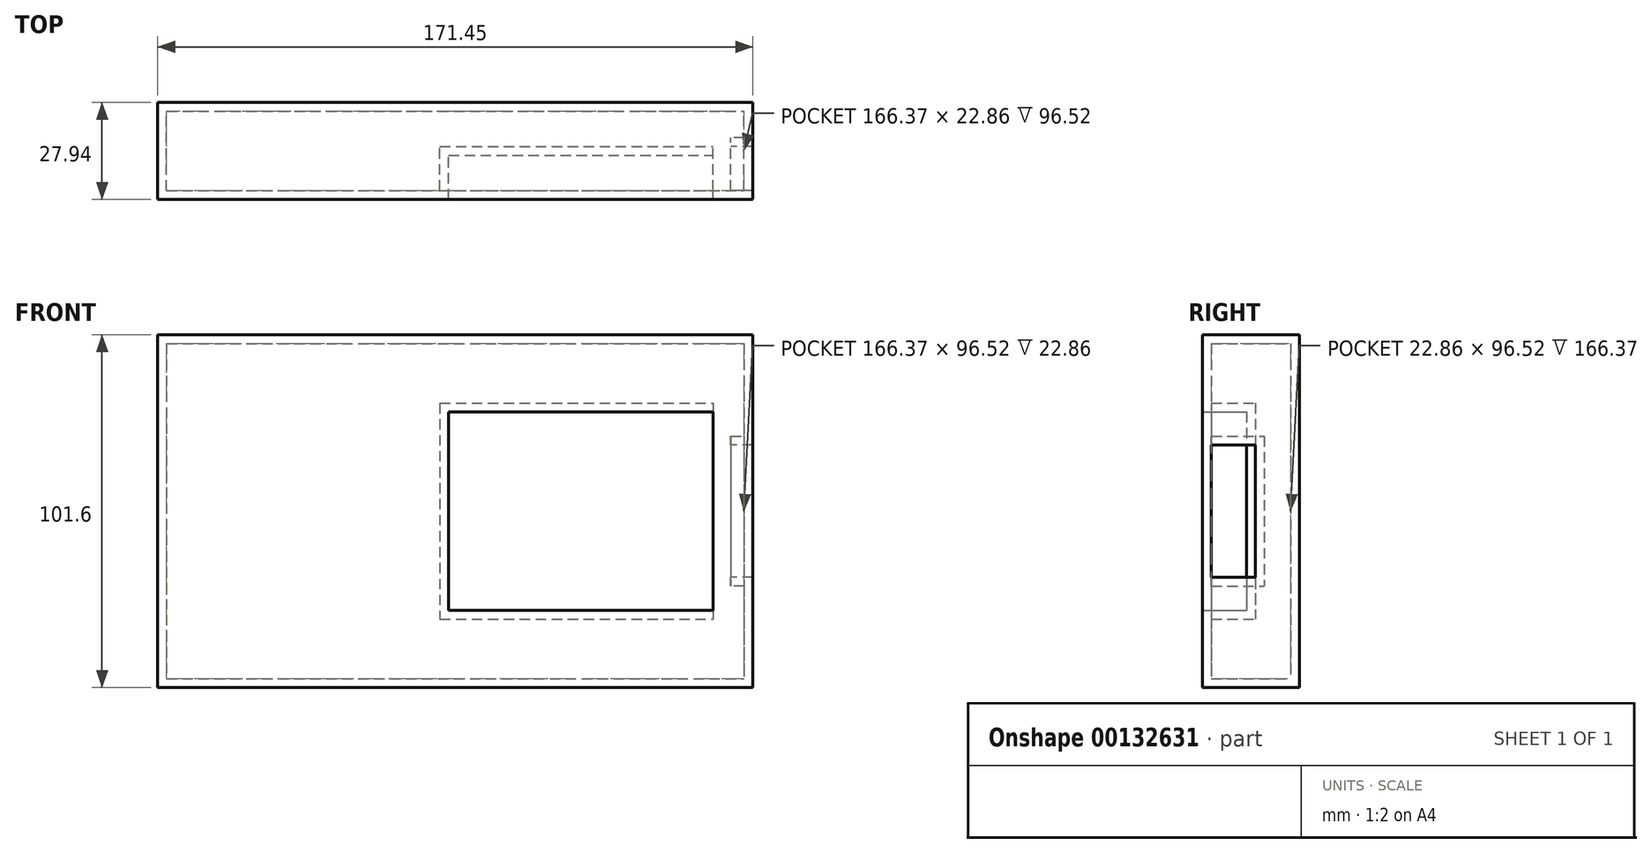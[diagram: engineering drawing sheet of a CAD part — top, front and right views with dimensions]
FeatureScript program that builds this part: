
annotation { "Feature Type Name" : "Feature", "Feature Type Description" : "" }
export const myFeature = defineFeature(function(context is Context, id is Id, definition is map)
    precondition{}
    {
        {
            var Q0;
            Q0=qCreatedBy(makeId("Front.planeOp"),FACE);
            var sketch = newSketch(context, id + "F0", { "sketchPlane" : qUnion([Q0])});
            skLineSegment(sketch, "E0.bottom", {"start": v(-70.48, 47.32) * mm, "end": v(94.62, 47.32) * mm});
            skLineSegment(sketch, "E0.top", {"start": v(-70.48, -54.28) * mm, "end": v(94.62, -54.28) * mm});
            skLineSegment(sketch, "E0.left", {"start": v(-70.48, 47.32) * mm, "end": v(-70.48, -54.28) * mm});
            skLineSegment(sketch, "E0.right", {"start": v(94.62, 47.32) * mm, "end": v(94.62, -54.28) * mm});
            skSolve(sketch);
        }
        {
            var Q0;
            Q0=makeQuery(id+"F0.imprint","IMPRINT",FACE,{"disambiguationData":[TD([[makeQuery(id+"F0.imprint","IMPRINT",EDGE,{"derivedFrom":sQuery(id+"F0.wireOp",EDGE,"E0.bottom")}),-1.0]])]});
            var Q1;
            Q1 = qSketchRegion(id + "F2", true);
            extrude(context, id + "F1", {"entities" : qUnion([Q0, Q1]), "depth" : 15.24 * mm});
        }
        {
            var Q0;
            Q0=makeQuery(id+"F1.opExtrude","CAP_FACE",FACE,{"disambiguationData":[OSD([sQuery(id+"F0.wireOp",EDGE,"E0.bottom"),sQuery(id+"F0.wireOp",EDGE,"E0.top"),sQuery(id+"F0.wireOp",EDGE,"E0.left"),sQuery(id+"F0.wireOp",EDGE,"E0.right")])],"isStart":false});
            var sketch = newSketch(context, id + "F2", { "sketchPlane" : qUnion([Q0])});
            skLineSegment(sketch, "E1.bottom", {"start": v(-70.48, 47.32) * mm, "end": v(94.62, 47.32) * mm});
            skLineSegment(sketch, "E1.top", {"start": v(-70.48, -54.28) * mm, "end": v(94.62, -54.28) * mm});
            skLineSegment(sketch, "E1.left", {"start": v(-70.48, 47.32) * mm, "end": v(-70.48, -54.28) * mm});
            skLineSegment(sketch, "E1.right", {"start": v(94.62, 47.32) * mm, "end": v(94.62, -54.28) * mm});
            skLineSegment(sketch, "E2.bottom", {"start": v(13.34, 25.1) * mm, "end": v(89.54, 25.1) * mm});
            skLineSegment(sketch, "E2.top", {"start": v(13.34, -32.06) * mm, "end": v(89.54, -32.06) * mm});
            skLineSegment(sketch, "E2.left", {"start": v(13.34, 25.1) * mm, "end": v(13.34, -32.06) * mm});
            skLineSegment(sketch, "E2.right", {"start": v(89.54, 25.1) * mm, "end": v(89.54, -32.06) * mm});
            skLineSegment(sketch, "E3", {"start": v(89.54, 0) * mm, "end": v(94.62, 0) * mm});
            skSolve(sketch);
        }
        {
            var Q0;
            Q0 = qSketchRegion(id + "F2", true);
            extrude(context, id + "F3", {"entities" : qUnion([Q0]), "operationType" : NewBodyOperationType.ADD, "depth" : 12.7 * mm});
        }
        {
            var Q0;
            Q0=makeQuery(id+"F3.boolean.opBoolean","MERGE",FACE,{"derivedFrom":[makeQuery(id+"F1.opExtrude","SWEPT_FACE",FACE,{"disambiguationData":[OSD([sQuery(id+"F0.wireOp",EDGE,"E0.right")])]}),makeQuery(id+"F3.opExtrude","SWEPT_FACE",FACE,{"disambiguationData":[OSD([sQuery(id+"F2.wireOp",EDGE,"E1.right")])]})]});
            var sketch = newSketch(context, id + "F4", { "sketchPlane" : qUnion([Q0])});
            skLineSegment(sketch, "E4.bottom", {"start": v(-25.4, 15.57) * mm, "end": v(-12.7, 15.57) * mm});
            skLineSegment(sketch, "E4.top", {"start": v(-25.4, -22.53) * mm, "end": v(-12.7, -22.53) * mm});
            skLineSegment(sketch, "E4.left", {"start": v(-25.4, 15.57) * mm, "end": v(-25.4, -22.53) * mm});
            skLineSegment(sketch, "E4.right", {"start": v(-12.7, 15.57) * mm, "end": v(-12.7, -22.53) * mm});
            skLineSegment(sketch, "E5.bottom", {"start": v(-27.94, 47.32) * mm, "end": v(0, 47.32) * mm});
            skLineSegment(sketch, "E5.top", {"start": v(-27.94, -54.28) * mm, "end": v(0, -54.28) * mm});
            skLineSegment(sketch, "E5.left", {"start": v(-27.94, 47.32) * mm, "end": v(-27.94, -54.28) * mm});
            skLineSegment(sketch, "E5.right", {"start": v(0, 47.32) * mm, "end": v(0, -54.28) * mm});
            skLineSegment(sketch, "E6", {"start": v(-13.97, 47.32) * mm, "end": v(-13.97, 15.57) * mm});
            skLineSegment(sketch, "E7", {"start": v(-12.7, -1.62) * mm, "end": v(0, -1.62) * mm});
            skSolve(sketch);
        }
        {
            var Q0;
            Q0 = qSketchRegion(id + "F4", true);
            extrude(context, id + "F5", {"entities" : qUnion([Q0]), "operationType" : NewBodyOperationType.ADD, "depth" : 6.35 * mm});
        }
        {
            var Q0;
            Q0=makeQuery(id+"F3.opExtrude","SWEPT_FACE",FACE,{"disambiguationData":[OSD([sQuery(id+"F2.wireOp",EDGE,"E2.right")])]});
            var sketch = newSketch(context, id + "F6", { "sketchPlane" : qUnion([Q0])});
            skLineSegment(sketch, "E8.bottom", {"start": v(15.24, 15.57) * mm, "end": v(24.13, 15.57) * mm});
            skLineSegment(sketch, "E8.top", {"start": v(15.24, -22.53) * mm, "end": v(24.13, -22.53) * mm});
            skLineSegment(sketch, "E8.left", {"start": v(15.24, 15.57) * mm, "end": v(15.24, -22.53) * mm});
            skLineSegment(sketch, "E8.right", {"start": v(24.13, 15.57) * mm, "end": v(24.13, -22.53) * mm});
            skLineSegment(sketch, "E9", {"start": v(21.6, 25.1) * mm, "end": v(21.6, 15.57) * mm});
            skSolve(sketch);
        }
        {
            var Q0;
            Q0 = qSketchRegion(id + "F6", true);
            extrude(context, id + "F7", {"entities" : qUnion([Q0]), "operationType" : NewBodyOperationType.ADD, "oppositeDirection" : true, "depth" : 5.08 * mm});
        }
        {
            var Q0;
            Q0=makeQuery(id+"F3.boolean.opBoolean","MERGE",FACE,{"derivedFrom":[makeQuery(id+"F1.opExtrude","SWEPT_FACE",FACE,{"disambiguationData":[OSD([sQuery(id+"F0.wireOp",EDGE,"E0.right")])]}),makeQuery(id+"F3.opExtrude","SWEPT_FACE",FACE,{"disambiguationData":[OSD([sQuery(id+"F2.wireOp",EDGE,"E1.right")])]})]});
            var Q1;
            Q1=makeQuery(id+"F3.opExtrude","SWEPT_FACE",FACE,{"disambiguationData":[OSD([sQuery(id+"F2.wireOp",EDGE,"E2.right")])]});
            shell(context, id + "F8", {"entities" : qUnion([Q0, Q1]), "thickness" : 2.54 * mm});
        }
    });
